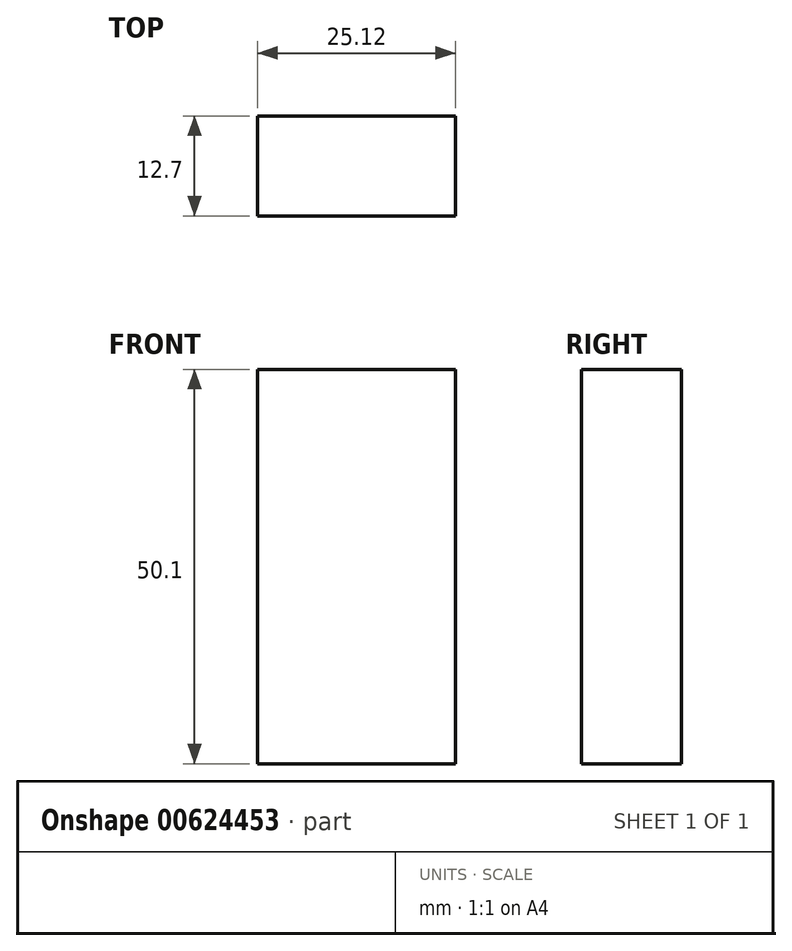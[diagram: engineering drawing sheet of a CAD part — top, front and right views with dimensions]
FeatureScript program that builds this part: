
annotation { "Feature Type Name" : "Feature", "Feature Type Description" : "" }
export const myFeature = defineFeature(function(context is Context, id is Id, definition is map)
    precondition{}
    {
        {
            var Q0;
            Q0=qCreatedBy(makeId("Front.planeOp"),FACE);
            var sketch = newSketch(context, id + "F0", { "sketchPlane" : qUnion([Q0])});
            skLineSegment(sketch, "E0.bottom", {"start": v(0, 0) * mm, "end": v(-25.12, 0) * mm});
            skLineSegment(sketch, "E0.top", {"start": v(0, 50.1) * mm, "end": v(-25.12, 50.1) * mm});
            skLineSegment(sketch, "E0.left", {"start": v(0, 0) * mm, "end": v(0, 50.1) * mm});
            skLineSegment(sketch, "E0.right", {"start": v(-25.12, 0) * mm, "end": v(-25.12, 50.1) * mm});
            skSolve(sketch);
        }
        {
            var Q0;
            Q0=makeQuery(id+"F0.imprint","IMPRINT",FACE,{"disambiguationData":[TD([[makeQuery(id+"F0.imprint","IMPRINT",EDGE,{"derivedFrom":sQuery(id+"F0.wireOp",EDGE,"E0.bottom")}),-1.0]])]});
            extrude(context, id + "F1", {"entities" : qUnion([Q0]), "depth" : 12.7 * mm, "offsetDistance" : 25 * mm});
        }
    });
